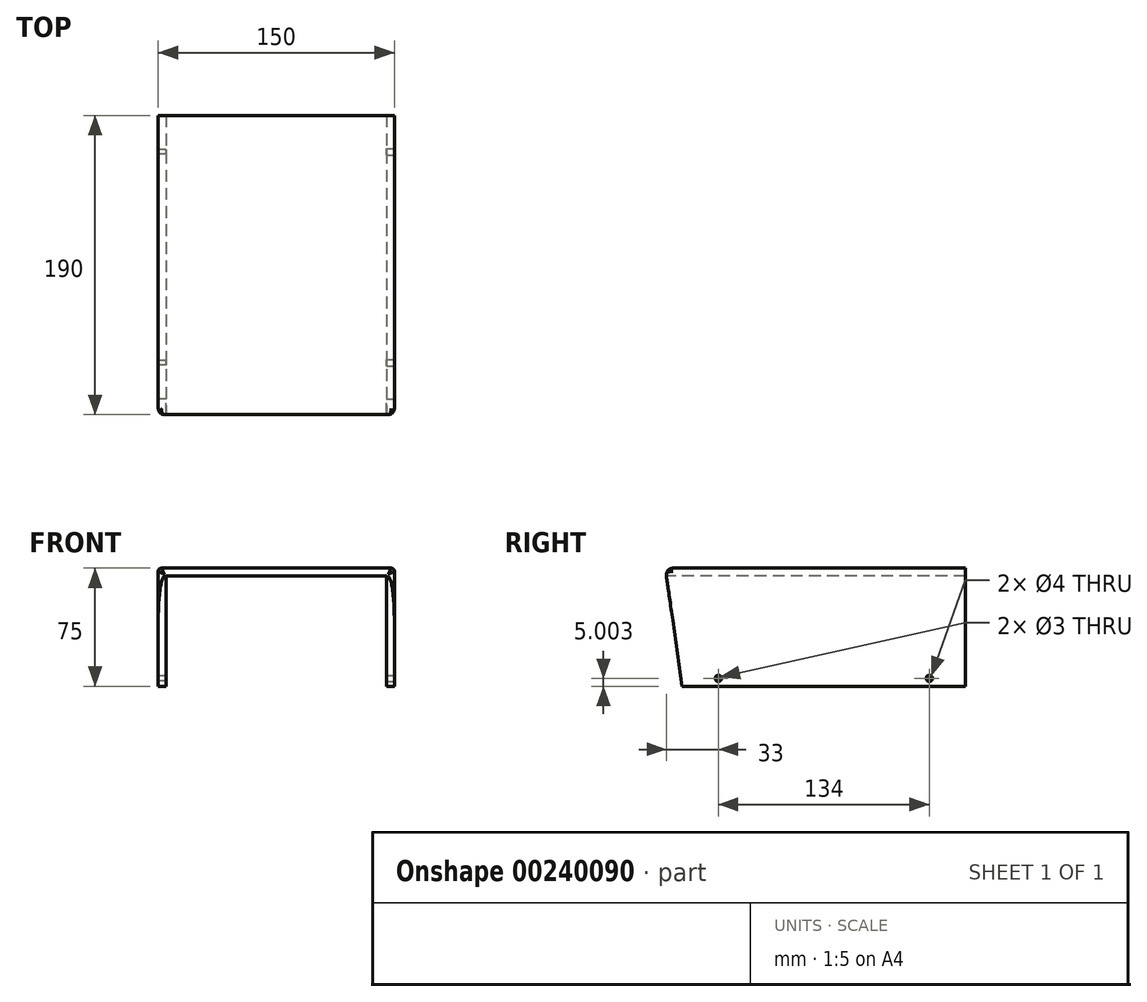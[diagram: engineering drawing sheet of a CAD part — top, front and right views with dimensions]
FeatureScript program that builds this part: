
annotation { "Feature Type Name" : "Feature", "Feature Type Description" : "" }
export const myFeature = defineFeature(function(context is Context, id is Id, definition is map)
    precondition{}
    {
        {
            var Q0;
            Q0=qCreatedBy(makeId("Front.planeOp"),FACE);
            var sketch = newSketch(context, id + "F0", { "sketchPlane" : qUnion([Q0])});
            skLineSegment(sketch, "E0", {"start": v(-75.84, 40.7) * mm, "end": v(74.16, 40.7) * mm});
            skLineSegment(sketch, "E1", {"start": v(74.16, 40.7) * mm, "end": v(74.16, -34.3) * mm});
            skLineSegment(sketch, "E2", {"start": v(74.16, -34.3) * mm, "end": v(69.16, -34.3) * mm});
            skLineSegment(sketch, "E3", {"start": v(69.16, -34.3) * mm, "end": v(69.16, 35.7) * mm});
            skLineSegment(sketch, "E4", {"start": v(69.16, 35.7) * mm, "end": v(-70.84, 35.7) * mm});
            skLineSegment(sketch, "E5", {"start": v(-70.84, 35.7) * mm, "end": v(-70.84, -34.3) * mm});
            skLineSegment(sketch, "E6", {"start": v(-70.84, -34.3) * mm, "end": v(-75.84, -34.3) * mm});
            skLineSegment(sketch, "E7", {"start": v(-75.84, -34.3) * mm, "end": v(-75.84, 40.7) * mm});
            skSolve(sketch);
        }
        {
            var Q0;
            Q0=makeQuery(id+"F0.imprint","IMPRINT",FACE,{"disambiguationData":[TD([[makeQuery(id+"F0.imprint","IMPRINT",EDGE,{"derivedFrom":sQuery(id+"F0.wireOp",EDGE,"E0")}),-1.0]])]});
            extrude(context, id + "F1", {"entities" : qUnion([Q0]), "oppositeDirection" : true, "depth" : 190 * mm});
        }
        {
            var Q0;
            Q0=makeQuery(id+"F1.opExtrude","SWEPT_FACE",FACE,{"disambiguationData":[OSD([sQuery(id+"F0.wireOp",EDGE,"E7")])]});
            var sketch = newSketch(context, id + "F2", { "sketchPlane" : qUnion([Q0])});
            skLineSegment(sketch, "E8", {"start": v(0, 35.54) * mm, "end": v(-10, -34.3) * mm});
            skLineSegment(sketch, "E9", {"start": v(-10, -34.3) * mm, "end": v(0, -34.3) * mm});
            skLineSegment(sketch, "E10", {"start": v(0, -34.3) * mm, "end": v(0, 35.54) * mm});
            skSolve(sketch);
        }
        {
            var Q0;
            Q0=makeQuery(id+"F2.imprint","IMPRINT",FACE,{"disambiguationData":[TD([[makeQuery(id+"F2.imprint","IMPRINT",EDGE,{"derivedFrom":sQuery(id+"F2.wireOp",EDGE,"E8")}),1.0]])]});
            extrude(context, id + "F3", {"entities" : qUnion([Q0]), "operationType" : NewBodyOperationType.REMOVE, "oppositeDirection" : true, "depth" : 25 * mm});
        }
        {
            var Q0;
            Q0=makeQuery(id+"F1.opExtrude","SWEPT_FACE",FACE,{"disambiguationData":[OSD([sQuery(id+"F0.wireOp",EDGE,"E1")])]});
            var sketch = newSketch(context, id + "F4", { "sketchPlane" : qUnion([Q0])});
            skLineSegment(sketch, "E11", {"start": v(0, 35.25) * mm, "end": v(10, -34.3) * mm});
            skLineSegment(sketch, "E12", {"start": v(10, -34.3) * mm, "end": v(0, -34.3) * mm});
            skLineSegment(sketch, "E13", {"start": v(0, -34.3) * mm, "end": v(0, 35.25) * mm});
            skSolve(sketch);
        }
        {
            var Q0;
            Q0=makeQuery(id+"F4.imprint","IMPRINT",FACE,{"disambiguationData":[TD([[makeQuery(id+"F4.imprint","IMPRINT",EDGE,{"derivedFrom":sQuery(id+"F4.wireOp",EDGE,"E11")}),-1.0]])]});
            extrude(context, id + "F5", {"entities" : qUnion([Q0]), "operationType" : NewBodyOperationType.REMOVE, "oppositeDirection" : true, "depth" : 25 * mm});
        }
        {
            var Q0;
            Q0=makeQuery(id+"F1.opExtrude","SWEPT_FACE",FACE,{"disambiguationData":[OSD([sQuery(id+"F0.wireOp",EDGE,"E1")])]});
            var sketch = newSketch(context, id + "F6", { "sketchPlane" : qUnion([Q0])});
            skCircle(sketch, "E14", {"center": v(167, -29.3) * mm, "radius": 2 * mm});
            skCircle(sketch, "E15", {"center": v(33, -29.3) * mm, "radius": 2 * mm});
            skSolve(sketch);
        }
        {
            var Q0;
            Q0=makeQuery(id+"F6.imprint","IMPRINT",FACE,{"disambiguationData":[TD([[makeQuery(id+"F6.imprint","IMPRINT",EDGE,{"derivedFrom":sQuery(id+"F6.wireOp",EDGE,"E15")}),1.0]])]});
            var Q1;
            Q1=makeQuery(id+"F6.imprint","IMPRINT",FACE,{"disambiguationData":[TD([[makeQuery(id+"F6.imprint","IMPRINT",EDGE,{"derivedFrom":sQuery(id+"F6.wireOp",EDGE,"E14")}),1.0]])]});
            extrude(context, id + "F7", {"entities" : qUnion([Q0, Q1]), "operationType" : NewBodyOperationType.REMOVE, "oppositeDirection" : true, "depth" : 25 * mm});
        }
        {
            var Q0;
            Q0=makeQuery(id+"F1.opExtrude","SWEPT_FACE",FACE,{"disambiguationData":[OSD([sQuery(id+"F0.wireOp",EDGE,"E7")])]});
            var sketch = newSketch(context, id + "F8", { "sketchPlane" : qUnion([Q0])});
            skCircle(sketch, "E16", {"center": v(-167, -29.3) * mm, "radius": 1.5 * mm});
            skCircle(sketch, "E17", {"center": v(-33, -29.3) * mm, "radius": 1.5 * mm});
            skSolve(sketch);
        }
        {
            var Q0;
            Q0=makeQuery(id+"F8.imprint","IMPRINT",FACE,{"disambiguationData":[TD([[makeQuery(id+"F8.imprint","IMPRINT",EDGE,{"derivedFrom":sQuery(id+"F8.wireOp",EDGE,"E16")}),1.0]])]});
            var Q1;
            Q1=makeQuery(id+"F8.imprint","IMPRINT",FACE,{"disambiguationData":[TD([[makeQuery(id+"F8.imprint","IMPRINT",EDGE,{"derivedFrom":sQuery(id+"F8.wireOp",EDGE,"E17")}),1.0]])]});
            extrude(context, id + "F9", {"entities" : qUnion([Q0, Q1]), "operationType" : NewBodyOperationType.REMOVE, "oppositeDirection" : true, "depth" : 25 * mm});
        }
        {
            var Q0;
            Q0=makeQuery(id+"F3.boolean.opBoolean","COPY",EDGE,{"derivedFrom":makeQuery(id+"F3.opExtrude","CAP_EDGE",EDGE,{"disambiguationData":[OSD([sQuery(id+"F2.wireOp",EDGE,"E8")])],"isStart":true})});
            var Q1;
            Q1=makeQuery(id+"F1.opExtrude","CAP_EDGE",EDGE,{"disambiguationData":[OSD([sQuery(id+"F0.wireOp",EDGE,"E7")])],"isStart":true});
            var Q2;
            Q2=makeQuery(id+"F1.opExtrude","CAP_EDGE",EDGE,{"disambiguationData":[OSD([sQuery(id+"F0.wireOp",EDGE,"E0")])],"isStart":true});
            var Q3;
            Q3=makeQuery(id+"F5.boolean.opBoolean","COPY",EDGE,{"derivedFrom":makeQuery(id+"F5.opExtrude","CAP_EDGE",EDGE,{"disambiguationData":[OSD([sQuery(id+"F4.wireOp",EDGE,"E11")])],"isStart":true})});
            var Q4;
            Q4=makeQuery(id+"F1.opExtrude","CAP_EDGE",EDGE,{"disambiguationData":[OSD([sQuery(id+"F0.wireOp",EDGE,"E1")])],"isStart":true});
            fillet(context, id + "F10", {"entities" : qUnion([Q0, Q1, Q2, Q3, Q4]), "radius" : 4 * mm, "tangentPropagation" : true, "allowEdgeOverflow" : false});
        }
        {
            var Q0;
            Q0=makeQuery(id+"F1.opExtrude","SWEPT_EDGE",EDGE,{"disambiguationData":[OSD([sQuery(id+"F0.wireOp",EDGE,"E0"),sQuery(id+"F0.wireOp",EDGE,"E1")])]});
            var Q1;
            Q1=makeQuery(id+"F1.opExtrude","SWEPT_EDGE",EDGE,{"disambiguationData":[OSD([sQuery(id+"F0.wireOp",EDGE,"E0"),sQuery(id+"F0.wireOp",EDGE,"E7")])]});
            fillet(context, id + "F11", {"entities" : qUnion([Q0, Q1]), "radius" : 2 * mm, "tangentPropagation" : true, "allowEdgeOverflow" : false});
        }
    });
